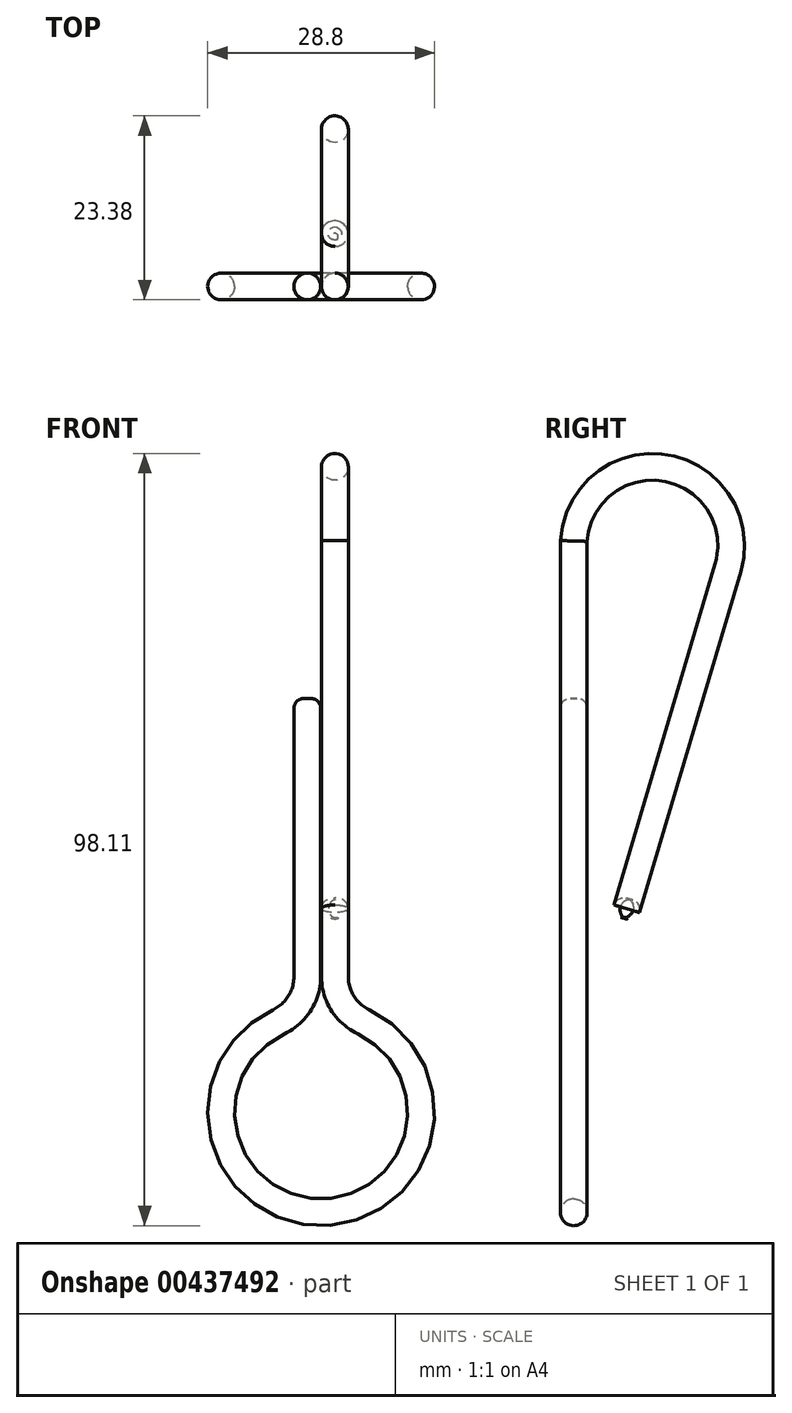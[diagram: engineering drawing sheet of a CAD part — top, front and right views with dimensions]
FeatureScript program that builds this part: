
annotation { "Feature Type Name" : "Feature", "Feature Type Description" : "" }
export const myFeature = defineFeature(function(context is Context, id is Id, definition is map)
    precondition{}
    {
        {
            var Q0;
            Q0=qCreatedBy(makeId("Front.planeOp"),FACE);
            var sketch = newSketch(context, id + "F0", { "sketchPlane" : qUnion([Q0])});
            skArc(sketch, "E0", {"start": v(-5.4, 11.5) * mm, "mid": v(0, -12.7) * mm, "end": v(5.4, 11.5) * mm});
            skLineSegment(sketch, "E1.bottom", {"start": v(-3.5, 36.38) * mm, "end": v(3.5, 36.38) * mm, "construction": true});
            skLineSegment(sketch, "E1.top", {"start": v(-3.5, 32.36) * mm, "end": v(3.5, 32.36) * mm, "construction": true});
            skLineSegment(sketch, "E1.left", {"start": v(-3.5, 36.38) * mm, "end": v(-3.5, 32.36) * mm, "construction": true});
            skLineSegment(sketch, "E1.right", {"start": v(3.5, 36.38) * mm, "end": v(3.5, 32.36) * mm, "construction": true});
            skPoint(sketch, "E1.middle", {"position": v(0, 34.37) * mm});
            skLineSegment(sketch, "E2", {"start": v(-3.5, 36.38) * mm, "end": v(0, 32.36) * mm, "construction": true});
            skLineSegment(sketch, "E3", {"start": v(0, 32.36) * mm, "end": v(-3.5, 32.36) * mm, "construction": true});
            skLineSegment(sketch, "E4", {"start": v(0, 36.38) * mm, "end": v(-3.5, 32.36) * mm, "construction": true});
            skLineSegment(sketch, "E5", {"start": v(3.5, 36.38) * mm, "end": v(0, 32.36) * mm, "construction": true});
            skLineSegment(sketch, "E6", {"start": v(0, 36.38) * mm, "end": v(3.5, 32.36) * mm, "construction": true});
            skLineSegment(sketch, "E7", {"start": v(-1.75, 17.24) * mm, "end": v(-1.75, 52.58) * mm});
            skPoint(sketch, "E7.startSnap0", {"position": v(-1.75, 34.37) * mm});
            skLineSegment(sketch, "E8", {"start": v(1.75, 72.58) * mm, "end": v(1.75, 17.24) * mm});
            skPoint(sketch, "E8.startSnap0", {"position": v(1.75, 34.37) * mm});
            skPoint(sketch, "E9.visualSharp", {"position": v(-1.75, 12.58) * mm});
            skArc(sketch, "E9.filletArc", {"start": v(-5.4, 11.5) * mm, "mid": v(-2.74, 13.84) * mm, "end": v(-1.75, 17.24) * mm});
            skPoint(sketch, "E10.visualSharp", {"position": v(1.75, 12.58) * mm});
            skArc(sketch, "E10.filletArc", {"start": v(1.75, 17.24) * mm, "mid": v(2.74, 13.84) * mm, "end": v(5.4, 11.5) * mm});
            skSolve(sketch);
        }
        {
            var Q0;
            Q0=qCreatedBy(makeId("Right.planeOp"),FACE);
            var Q1;
            Q1=sQuery(id+"F0.wireOp",VERTEX,"E8.start");
            cPlane(context, id + "F1", {"entities" : qUnion([Q0, Q1]), "cplaneType" : CPlaneType.PLANE_POINT, "offset" : 25.4 * mm, "width" : 152.4 * mm, "height" : 152.4 * mm});
        }
        {
            var Q0;
            Q0=qCreatedBy(id+"F1.planeOp",FACE);
            var sketch = newSketch(context, id + "F2", { "sketchPlane" : qUnion([Q0])});
            skArc(sketch, "E11", {"start": v(19.57, 69.16) * mm, "mid": v(11.7, 81.86) * mm, "end": v(0, 72.58) * mm});
            skPoint(sketch, "E11.first.point", {"position": v(0, 72.58) * mm});
            skPoint(sketch, "E11.second.point", {"position": v(19.98, 71.7) * mm});
            skPoint(sketch, "E11.third.point", {"position": v(19.98, 72.32) * mm});
            skLineSegment(sketch, "E12", {"start": v(6.36, 24.65) * mm, "end": v(19.57, 69.16) * mm});
            skLineSegment(sketch, "E13", {"start": v(0, 72.58) * mm, "end": v(25.18, 72.58) * mm, "construction": true});
            skSolve(sketch);
        }
        {
            var Q0;
            Q0=qCreatedBy(makeId("Top.planeOp"),FACE);
            var Q1;
            Q1=sQuery(id+"F0.wireOp",VERTEX,"E7.end");
            cPlane(context, id + "F3", {"entities" : qUnion([Q0, Q1]), "cplaneType" : CPlaneType.PLANE_POINT, "offset" : 25.4 * mm, "width" : 152.4 * mm, "height" : 152.4 * mm});
        }
        {
            var Q0;
            Q0=qCreatedBy(id+"F3.planeOp",FACE);
            var sketch = newSketch(context, id + "F4", { "sketchPlane" : qUnion([Q0])});
            skCircle(sketch, "E14", {"center": v(-1.75, 0) * mm, "radius": 1.7 * mm});
            skSolve(sketch);
        }
        {
            var Q0;
            Q0=makeQuery(id+"F4.imprint","IMPRINT",FACE,{"disambiguationData":[TD([[makeQuery(id+"F4.imprint","IMPRINT",EDGE,{"derivedFrom":sQuery(id+"F4.wireOp",EDGE,"E14")}),1.0]])]});
            var Q1;
            Q1=sQuery(id+"F4.wireOp",EDGE,"E14");
            var Q2;
            Q2=sQuery(id+"F0.wireOp",EDGE,"E7");
            var Q3;
            Q3=sQuery(id+"F0.wireOp",EDGE,"E9.filletArc");
            var Q4;
            Q4=sQuery(id+"F0.wireOp",EDGE,"E0");
            var Q5;
            Q5=sQuery(id+"F0.wireOp",EDGE,"E10.filletArc");
            var Q6;
            Q6=sQuery(id+"F0.wireOp",EDGE,"E8");
            var Q7;
            Q7=sQuery(id+"F2.wireOp",EDGE,"E11");
            var Q8;
            Q8=sQuery(id+"F2.wireOp",EDGE,"E12");
            sweep(context, id + "F5", {"profiles" : qUnion([Q0]), "surfaceProfiles" : qUnion([Q1]), "path" : qUnion([Q2, Q3, Q4, Q5, Q6, Q7, Q8])});
        }
        {
            var Q0;
            Q0=makeQuery(id+"F5.opSweep","CAP_EDGE",EDGE,{"disambiguationData":[OSD([sQuery(id+"F2.wireOp",VERTEX,"E12.start"),sQuery(id+"F4.wireOp",EDGE,"E14")])],"isStart":false});
            var Q1;
            Q1=makeQuery(id+"F5.opSweep","CAP_EDGE",EDGE,{"disambiguationData":[OSD([sQuery(id+"F0.wireOp",VERTEX,"E7.end"),sQuery(id+"F4.wireOp",EDGE,"E14")])],"isStart":true});
            fillet(context, id + "F6", {"entities" : qUnion([Q0, Q1]), "radius" : 1.27 * mm, "tangentPropagation" : true, "allowEdgeOverflow" : false});
        }
    });
